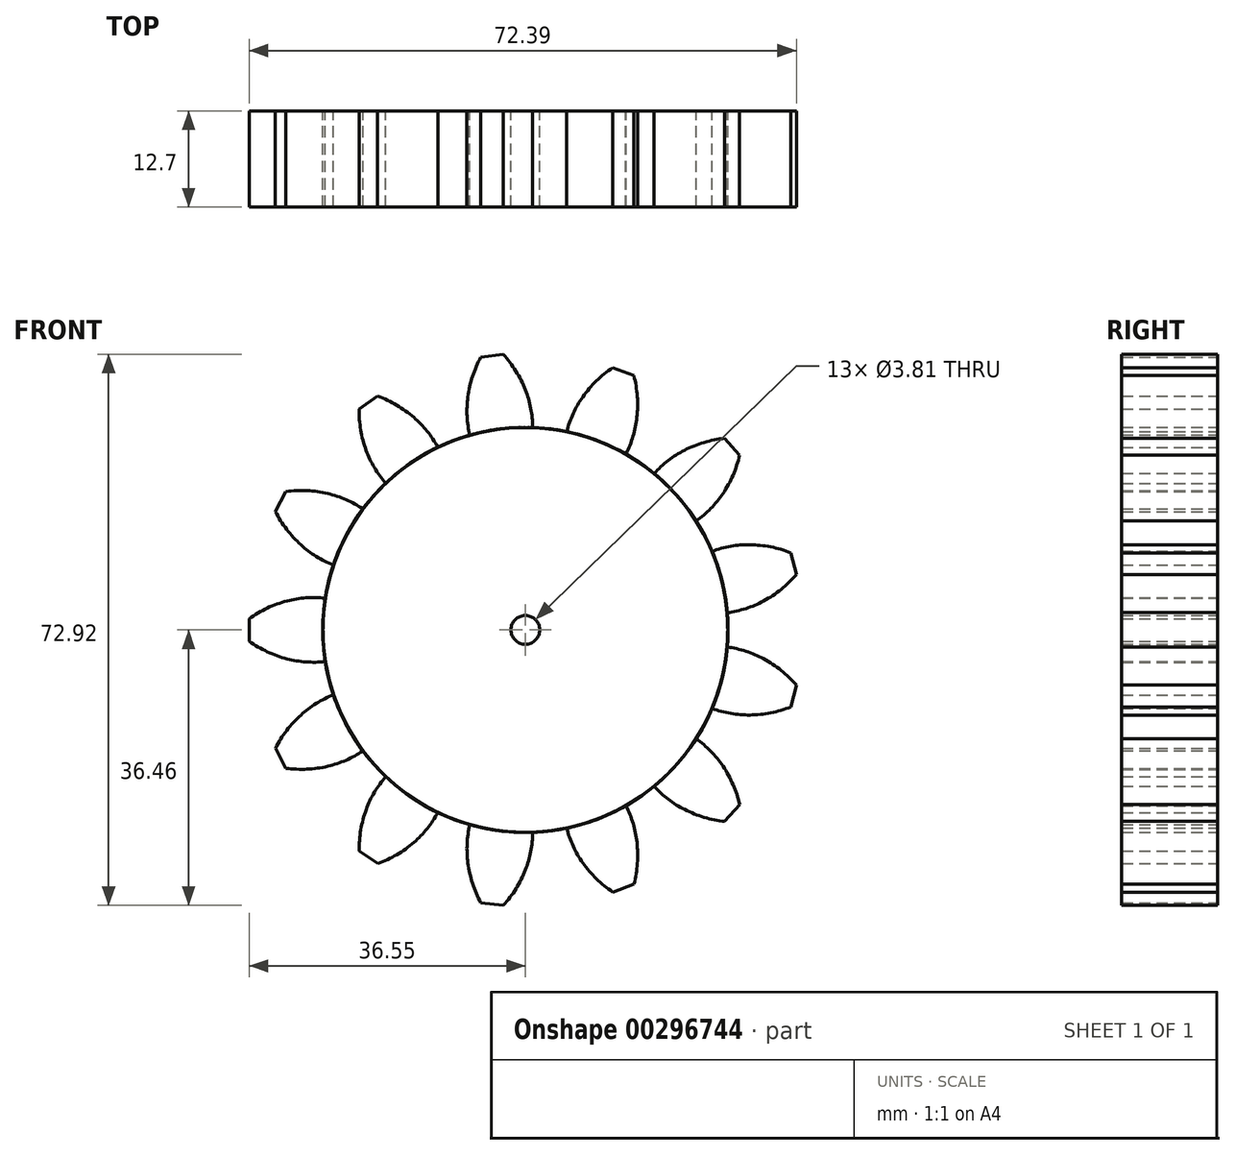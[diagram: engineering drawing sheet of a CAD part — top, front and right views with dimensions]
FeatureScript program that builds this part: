
annotation { "Feature Type Name" : "Feature", "Feature Type Description" : "" }
export const myFeature = defineFeature(function(context is Context, id is Id, definition is map)
    precondition{}
    {
        {
            var Q0;
            Q0=qCreatedBy(makeId("Front.planeOp"),FACE);
            var sketch = newSketch(context, id + "F0", { "sketchPlane" : qUnion([Q0])});
            skCircle(sketch, "E0", {"center": v(0, 0) * mm, "radius": 31.75 * mm, "construction": true});
            skCircle(sketch, "E1", {"center": v(0, 0) * mm, "radius": 36.58 * mm, "construction": true});
            skCircle(sketch, "E2", {"center": v(0, 0) * mm, "radius": 26.8 * mm});
            skLineSegment(sketch, "E3", {"start": v(0, 0) * mm, "end": v(0, 83.58) * mm, "construction": true});
            skLineSegment(sketch, "E4", {"start": v(0, 0) * mm, "end": v(-10.06, 82.74) * mm, "construction": true});
            skLineSegment(sketch, "E5", {"start": v(0, 31.75) * mm, "end": v(-54.38, 31.75) * mm, "construction": true});
            skLineSegment(sketch, "E6", {"start": v(-54.38, 31.75) * mm, "end": v(0, 31.75) * mm, "construction": true});
            skLineSegment(sketch, "E7", {"start": v(0, 31.75) * mm, "end": v(-51, 13.19) * mm, "construction": true});
            skCircle(sketch, "E8", {"center": v(0, 31.75) * mm, "radius": 14.6 * mm, "construction": true});
            skCircle(sketch, "E9", {"center": v(0, 0) * mm, "radius": 29.84 * mm, "construction": true});
            skCircle(sketch, "E10", {"center": v(-13.64, 26.53) * mm, "radius": 14.6 * mm, "construction": true});
            skArc(sketch, "E11", {"start": v(0, 31.75) * mm, "mid": v(-1.25, 34.24) * mm, "end": v(-2.93, 36.46) * mm});
            skArc(sketch, "E12", {"start": v(0.96, 26.78) * mm, "mid": v(0.7, 29.3) * mm, "end": v(0, 31.75) * mm});
            skArc(sketch, "E13.MirrorCS", {"start": v(-7.6, 30.83) * mm, "mid": v(-6.99, 33.54) * mm, "end": v(-5.9, 36.1) * mm});
            skArc(sketch, "E14.MirrorCS", {"start": v(-7.35, 25.77) * mm, "mid": v(-7.7, 28.29) * mm, "end": v(-7.6, 30.83) * mm});
            skLineSegment(sketch, "E15", {"start": v(-5.9, 36.1) * mm, "end": v(-2.93, 36.46) * mm});
            skCircle(sketch, "E16", {"center": v(0, 0) * mm, "radius": 1.9 * mm});
            skSolve(sketch);
        }
        {
            var Q0;
            {var subQ0=sQuery(id+"F0.wireOp",EDGE,"E2");var subQ1=makeQuery(id+"F0.imprint","INTERSECT",VERTEX,{"derivedFrom":[subQ0,sQuery(id+"F0.wireOp",EDGE,"E12")]});Q0=makeQuery(id+"F0.imprint","IMPRINT",FACE,{"disambiguationData":[TD([[makeQuery(id+"F0.imprint","IMPRINT",EDGE,{"disambiguationData":[TD([[subQ1,-1.0]])],"derivedFrom":subQ0}),1.0]])]});}
            var Q1;
            Q1=makeQuery(id+"F0.imprint","IMPRINT",FACE,{"disambiguationData":[TD([[makeQuery(id+"F0.imprint","IMPRINT",EDGE,{"derivedFrom":sQuery(id+"F0.wireOp",EDGE,"E11")}),1.0]])]});
            extrude(context, id + "F1", {"entities" : qUnion([Q0, Q1]), "depth" : 12.7 * mm});
        }
        {
            var Q0;
            Q0=makeQuery(id+"F1.opExtrude","SWEPT_BODY",BODY,{"disambiguationData":[OSD([sQuery(id+"F0.wireOp",EDGE,"E2"),sQuery(id+"F0.wireOp",EDGE,"E11"),sQuery(id+"F0.wireOp",EDGE,"E12"),sQuery(id+"F0.wireOp",EDGE,"E13.MirrorCS"),sQuery(id+"F0.wireOp",EDGE,"E14.MirrorCS"),sQuery(id+"F0.wireOp",EDGE,"E15")])]});
            var Q1;
            Q1=makeQuery(id+"F1.opExtrude","SWEPT_FACE",FACE,{"disambiguationData":[OSD([sQuery(id+"F0.wireOp",EDGE,"E2")])]});
            circularPattern(context, id + "F2", {"entities" : qUnion([Q0]), "axis" : qUnion([Q1]), "angle" : 360 * degree, "instanceCount" : 13, "equalSpace" : true});
        }
    });
